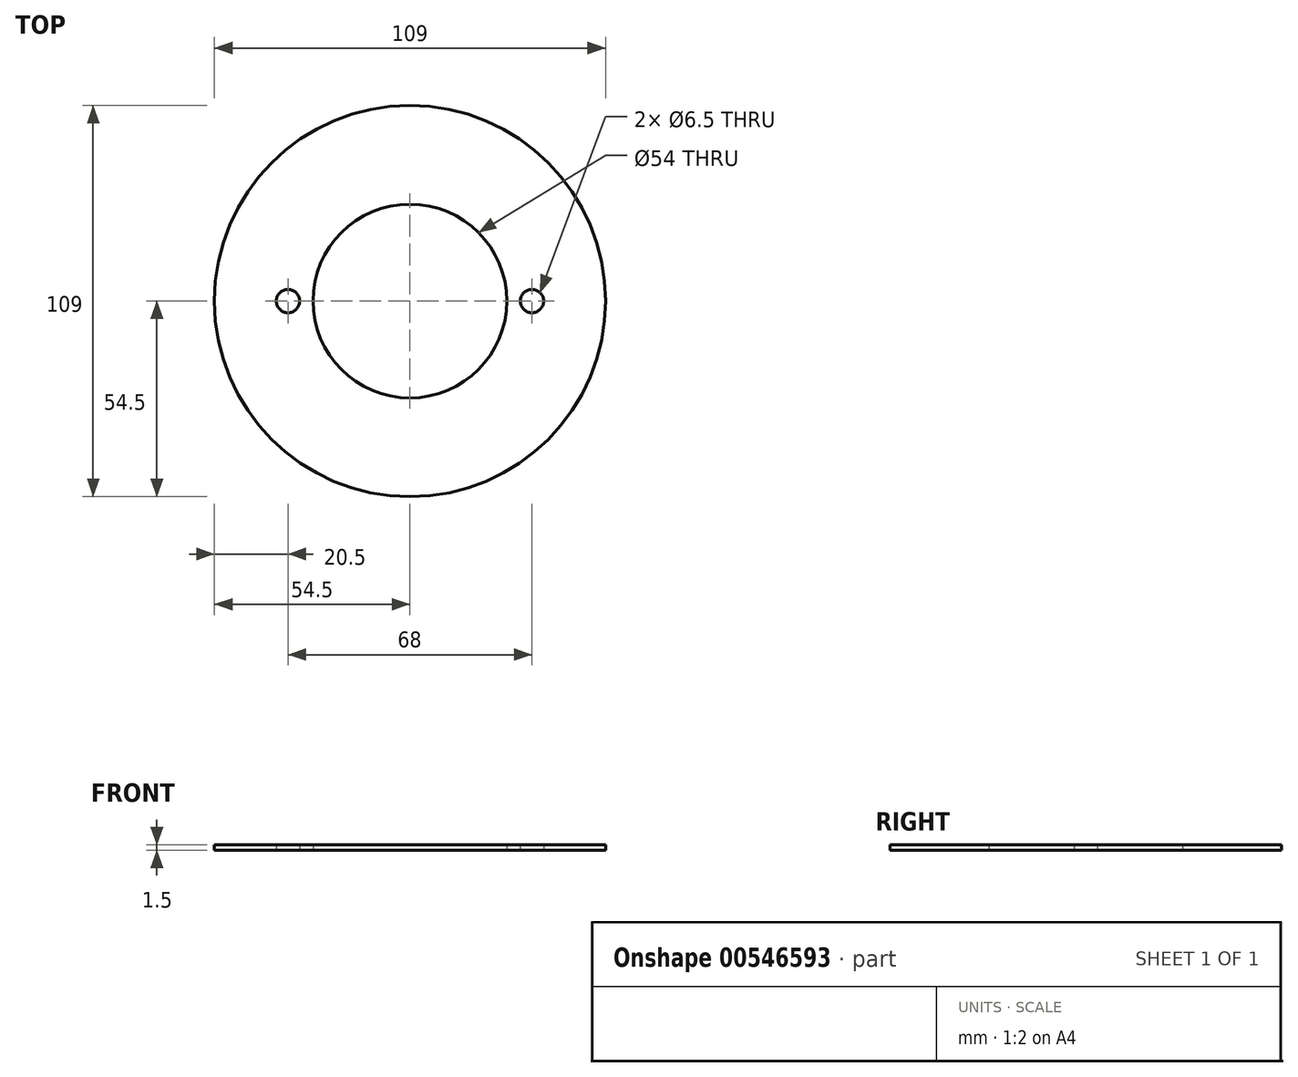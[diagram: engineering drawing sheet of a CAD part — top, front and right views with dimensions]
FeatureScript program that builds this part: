
annotation { "Feature Type Name" : "Feature", "Feature Type Description" : "" }
export const myFeature = defineFeature(function(context is Context, id is Id, definition is map)
    precondition{}
    {
        {
            var Q0;
            Q0=qCreatedBy(makeId("Top.planeOp"),FACE);
            var sketch = newSketch(context, id + "F0", { "sketchPlane" : qUnion([Q0])});
            skCircle(sketch, "E0", {"center": v(0, 0) * mm, "radius": 54.5 * mm});
            skCircle(sketch, "E1", {"center": v(0, 0) * mm, "radius": 27 * mm});
            skCircle(sketch, "E2", {"center": v(-34, 0) * mm, "radius": 3.25 * mm});
            skCircle(sketch, "E3.MirrorC", {"center": v(34, 0) * mm, "radius": 3.25 * mm});
            skSolve(sketch);
        }
        {
            var Q0;
            Q0=makeQuery(id+"F0.imprint","IMPRINT",FACE,{"disambiguationData":[TD([[makeQuery(id+"F0.imprint","IMPRINT",EDGE,{"derivedFrom":sQuery(id+"F0.wireOp",EDGE,"E0")}),1.0]])]});
            extrude(context, id + "F1", {"entities" : qUnion([Q0]), "depth" : 1.5 * mm, "offsetDistance" : 25 * mm});
        }
    });
